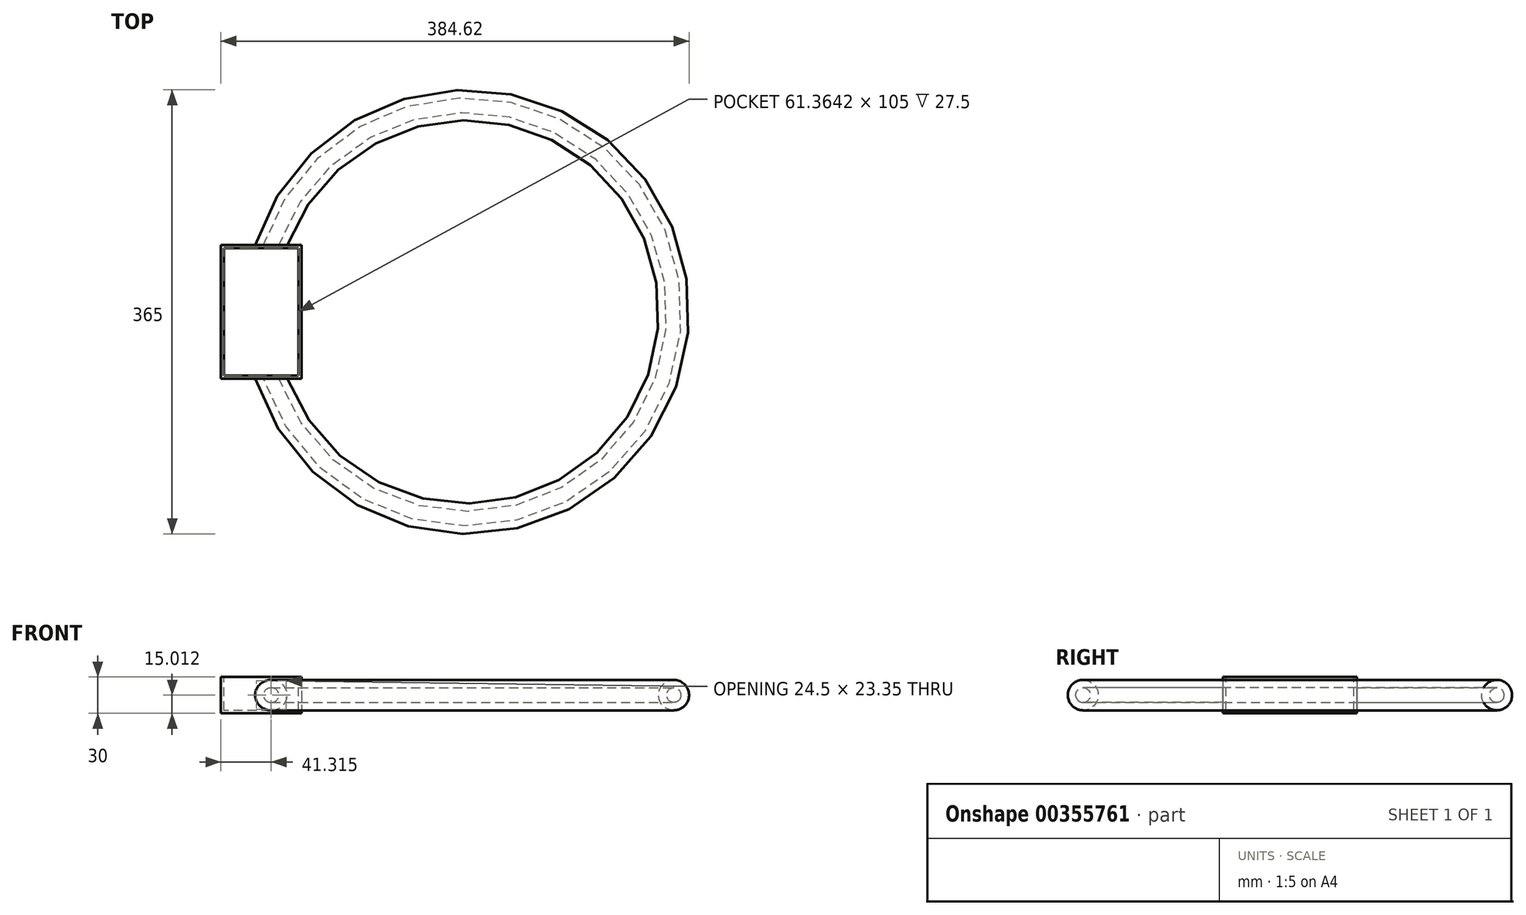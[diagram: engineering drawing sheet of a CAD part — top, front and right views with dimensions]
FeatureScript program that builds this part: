
annotation { "Feature Type Name" : "Feature", "Feature Type Description" : "" }
export const myFeature = defineFeature(function(context is Context, id is Id, definition is map)
    precondition{}
    {
        {
            var Q0;
            Q0=qCreatedBy(makeId("Front.planeOp"),FACE);
            var sketch = newSketch(context, id + "F0", { "sketchPlane" : qUnion([Q0])});
            skCircle(sketch, "E0", {"center": v(-170, 0) * mm, "radius": 12.5 * mm});
            skCircle(sketch, "E1.0", {"center": v(-170, 0) * mm, "radius": 6 * mm});
            skLineSegment(sketch, "E2", {"start": v(0, 35) * mm, "end": v(0, -35) * mm, "construction": true});
            skSolve(sketch);
        }
        {
            var Q0;
            Q0=makeQuery(id+"F0.imprint","IMPRINT",FACE,{"disambiguationData":[TD([[makeQuery(id+"F0.imprint","IMPRINT",EDGE,{"derivedFrom":sQuery(id+"F0.wireOp",EDGE,"E0")}),1.0]])]});
            var Q1;
            Q1=sQuery(id+"F0.wireOp",EDGE,"E2");
            revolve(context, id + "F1", {"entities" : qUnion([Q0]), "axis" : qUnion([Q1]), "revolveType" : RevolveType.FULL});
        }
        {
            var Q0;
            Q0=qCreatedBy(makeId("Top.planeOp"),FACE);
            var sketch = newSketch(context, id + "F2", { "sketchPlane" : qUnion([Q0])});
            skLineSegment(sketch, "E3", {"start": v(0, 55) * mm, "end": v(0, -55) * mm, "construction": true});
            skLineSegment(sketch, "E4", {"start": v(0, -55) * mm, "end": v(-220, -55) * mm, "construction": true});
            skLineSegment(sketch, "E5", {"start": v(-220, -55) * mm, "end": v(-220, 55) * mm, "construction": true});
            skLineSegment(sketch, "E6", {"start": v(0, 55) * mm, "end": v(-220, 55) * mm, "construction": true});
            skLineSegment(sketch, "E7", {"start": v(0, 0) * mm, "end": v(-220, 0) * mm, "construction": true});
            skLineSegment(sketch, "E8", {"start": v(-143.97, 55) * mm, "end": v(-143.97, -55) * mm, "construction": true});
            skLineSegment(sketch, "E9", {"start": v(-184.82, 55) * mm, "end": v(-184.82, -55) * mm, "construction": true});
            skLineSegment(sketch, "E10.bottom", {"start": v(-184.82, 55) * mm, "end": v(-143.97, 55) * mm});
            skLineSegment(sketch, "E10.top", {"start": v(-184.82, -55) * mm, "end": v(-143.97, -55) * mm});
            skLineSegment(sketch, "E10.left", {"start": v(-184.82, 55) * mm, "end": v(-184.82, -55) * mm});
            skLineSegment(sketch, "E10.right", {"start": v(-143.97, 55) * mm, "end": v(-143.97, -55) * mm});
            skLineSegment(sketch, "E11", {"start": v(-164.4, 55) * mm, "end": v(-164.4, -55) * mm, "construction": true});
            skLineSegment(sketch, "E12.bottom", {"start": v(-202.12, 55) * mm, "end": v(-135.34, 55) * mm});
            skLineSegment(sketch, "E12.top", {"start": v(-202.12, -55) * mm, "end": v(-135.34, -55) * mm});
            skLineSegment(sketch, "E12.left", {"start": v(-202.12, 55) * mm, "end": v(-202.12, -55) * mm});
            skLineSegment(sketch, "E12.right", {"start": v(-135.34, 55) * mm, "end": v(-135.34, -55) * mm});
            skSolve(sketch);
        }
        {
            var Q0;
            Q0 = qSketchRegion(id + "F2", true);
            extrude(context, id + "F3", {"entities" : qUnion([Q0]), "operationType" : NewBodyOperationType.REMOVE, "endBound" : BoundingType.SYMMETRIC, "depth" : 25 * mm});
        }
        {
            var Q0;
            Q0=qCreatedBy(makeId("Top.planeOp"),FACE);
            var sketch = newSketch(context, id + "F4", { "sketchPlane" : qUnion([Q0])});
            skLineSegment(sketch, "E13", {"start": v(-0.41, 55) * mm, "end": v(-0.41, -55) * mm, "construction": true});
            skLineSegment(sketch, "E14", {"start": v(-0.41, -55) * mm, "end": v(-220, -55) * mm, "construction": true});
            skLineSegment(sketch, "E15", {"start": v(-220, -55) * mm, "end": v(-220, 55) * mm, "construction": true});
            skLineSegment(sketch, "E16", {"start": v(-0.41, 55) * mm, "end": v(-220, 55) * mm, "construction": true});
            skLineSegment(sketch, "E17", {"start": v(0, 0) * mm, "end": v(-220, 0) * mm, "construction": true});
            skLineSegment(sketch, "E18", {"start": v(-144.38, 55) * mm, "end": v(-144.38, -55) * mm, "construction": true});
            skLineSegment(sketch, "E19", {"start": v(-185.23, 55) * mm, "end": v(-185.23, -55) * mm, "construction": true});
            skLineSegment(sketch, "E20.bottom", {"start": v(-185.23, 55) * mm, "end": v(-144.38, 55) * mm});
            skLineSegment(sketch, "E20.top", {"start": v(-185.23, -55) * mm, "end": v(-144.38, -55) * mm});
            skLineSegment(sketch, "E20.left", {"start": v(-185.23, 55) * mm, "end": v(-185.23, -55) * mm});
            skLineSegment(sketch, "E20.right", {"start": v(-144.38, 55) * mm, "end": v(-144.38, -55) * mm});
            skLineSegment(sketch, "E21", {"start": v(-164.8, 55) * mm, "end": v(-164.8, -55) * mm, "construction": true});
            skLineSegment(sketch, "E22.bottom", {"start": v(-202.12, 55) * mm, "end": v(-135.76, 55) * mm});
            skLineSegment(sketch, "E22.top", {"start": v(-202.12, -55) * mm, "end": v(-135.76, -55) * mm});
            skLineSegment(sketch, "E22.left", {"start": v(-202.12, 55) * mm, "end": v(-202.12, -55) * mm});
            skLineSegment(sketch, "E22.right", {"start": v(-135.76, 55) * mm, "end": v(-135.76, -55) * mm});
            skSolve(sketch);
        }
        {
            var Q0;
            Q0 = qSketchRegion(id + "F4", true);
            extrude(context, id + "F5", {"entities" : qUnion([Q0]), "operationType" : NewBodyOperationType.ADD, "endBound" : BoundingType.SYMMETRIC, "depth" : 30 * mm});
        }
        {
            var Q0;
            Q0=makeQuery(id+"F5.opExtrude","CAP_FACE",FACE,{"disambiguationData":[OSD([sQuery(id+"F4.wireOp",EDGE,"E22.bottom"),sQuery(id+"F4.wireOp",EDGE,"E22.top"),sQuery(id+"F4.wireOp",EDGE,"E22.left"),sQuery(id+"F4.wireOp",EDGE,"E22.right")])],"isStart":false});
            var sketch = newSketch(context, id + "F6", { "sketchPlane" : qUnion([Q0])});
            skLineSegment(sketch, "E23.0", {"start": v(-199.62, 52.5) * mm, "end": v(-199.62, -52.5) * mm});
            skLineSegment(sketch, "E23.1", {"start": v(-138.26, 52.5) * mm, "end": v(-199.62, 52.5) * mm});
            skLineSegment(sketch, "E23.2", {"start": v(-138.26, -52.5) * mm, "end": v(-138.26, 52.5) * mm});
            skLineSegment(sketch, "E23.3", {"start": v(-199.62, -52.5) * mm, "end": v(-138.26, -52.5) * mm});
            skSolve(sketch);
        }
        {
            var Q0;
            Q0=makeQuery(id+"F6.imprint","IMPRINT",FACE,{"disambiguationData":[TD([[makeQuery(id+"F6.imprint","IMPRINT",EDGE,{"derivedFrom":sQuery(id+"F6.wireOp",EDGE,"E23.0")}),1.0]])]});
            extrude(context, id + "F7", {"entities" : qUnion([Q0]), "operationType" : NewBodyOperationType.REMOVE, "oppositeDirection" : true, "depth" : 27.5 * mm});
        }
    });
